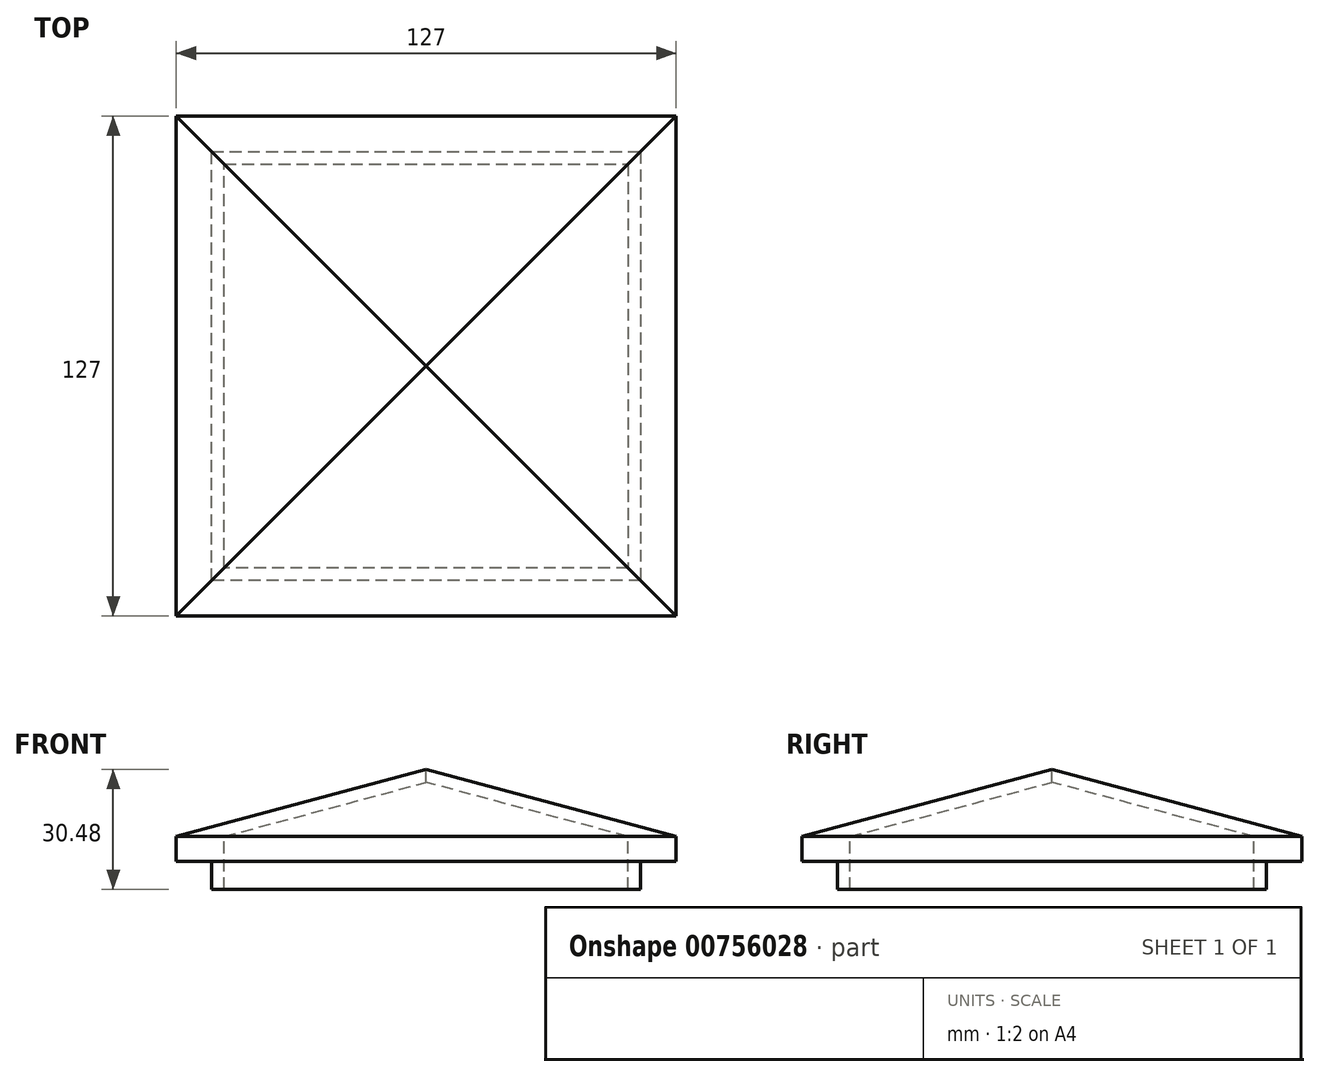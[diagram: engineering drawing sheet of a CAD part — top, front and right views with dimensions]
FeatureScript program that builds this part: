
annotation { "Feature Type Name" : "Feature", "Feature Type Description" : "" }
export const myFeature = defineFeature(function(context is Context, id is Id, definition is map)
    precondition{}
    {
        {
            var Q0;
            Q0=qCreatedBy(makeId("Front.planeOp"),FACE);
            var sketch = newSketch(context, id + "F0", { "sketchPlane" : qUnion([Q0])});
            skLineSegment(sketch, "E0", {"start": v(0, 30.48) * mm, "end": v(63.5, 13.47) * mm});
            skLineSegment(sketch, "E1", {"start": v(63.5, 13.47) * mm, "end": v(63.5, 7.12) * mm});
            skLineSegment(sketch, "E2", {"start": v(63.5, 7.12) * mm, "end": v(54.48, 7.12) * mm});
            skLineSegment(sketch, "E3", {"start": v(54.48, 7.12) * mm, "end": v(54.48, 0) * mm});
            skLineSegment(sketch, "E4", {"start": v(54.48, 0) * mm, "end": v(51.3, 0) * mm});
            skLineSegment(sketch, "E5", {"start": v(51.3, 0) * mm, "end": v(51.3, 13.45) * mm});
            skLineSegment(sketch, "E6", {"start": v(51.3, 13.45) * mm, "end": v(0, 27.2) * mm});
            skLineSegment(sketch, "E7", {"start": v(0, 27.2) * mm, "end": v(0, 30.48) * mm});
            skSolve(sketch);
        }
        {
            var Q0;
            Q0=makeQuery(id+"F0.imprint","IMPRINT",FACE,{"disambiguationData":[TD([[makeQuery(id+"F0.imprint","IMPRINT",EDGE,{"derivedFrom":sQuery(id+"F0.wireOp",EDGE,"E0")}),-1.0]])]});
            extrude(context, id + "F1", {"entities" : qUnion([Q0]), "oppositeDirection" : true, "depth" : 63.5 * mm, "offsetDistance" : 25.4 * mm});
        }
        {
            var Q0;
            Q0=qCreatedBy(makeId("Top.planeOp"),FACE);
            var sketch = newSketch(context, id + "F2", { "sketchPlane" : qUnion([Q0])});
            skLineSegment(sketch, "E8", {"start": v(0, 0) * mm, "end": v(63.5, 63.5) * mm});
            skLineSegment(sketch, "E9", {"start": v(63.5, 63.5) * mm, "end": v(0, 63.5) * mm});
            skLineSegment(sketch, "E10", {"start": v(0, 63.5) * mm, "end": v(0, 0) * mm});
            skSolve(sketch);
        }
        {
            var Q0;
            Q0 = qSketchRegion(id + "F2", true);
            extrude(context, id + "F3", {"entities" : qUnion([Q0]), "operationType" : NewBodyOperationType.REMOVE, "endBound" : BoundingType.THROUGH_ALL, "depth" : 25.4 * mm, "offsetDistance" : 25.4 * mm});
        }
        {
            var Q0;
            Q0=makeQuery(id+"F1.opExtrude","SWEPT_BODY",BODY,{"disambiguationData":[OSD([sQuery(id+"F0.wireOp",EDGE,"E0"),sQuery(id+"F0.wireOp",EDGE,"E1"),sQuery(id+"F0.wireOp",EDGE,"E2"),sQuery(id+"F0.wireOp",EDGE,"E3"),sQuery(id+"F0.wireOp",EDGE,"E4"),sQuery(id+"F0.wireOp",EDGE,"E5"),sQuery(id+"F0.wireOp",EDGE,"E6"),sQuery(id+"F0.wireOp",EDGE,"E7")])]});
            var Q1;
            Q1=qCreatedBy(makeId("Front.planeOp"),FACE);
            mirror(context, id + "F4", {"operationType" : NewBodyOperationType.ADD, "entities" : qUnion([Q0]), "mirrorPlane" : qUnion([Q1])});
        }
        {
            var Q0;
            Q0=makeQuery(id+"F1.opExtrude","SWEPT_BODY",BODY,{"disambiguationData":[OSD([sQuery(id+"F0.wireOp",EDGE,"E0"),sQuery(id+"F0.wireOp",EDGE,"E1"),sQuery(id+"F0.wireOp",EDGE,"E2"),sQuery(id+"F0.wireOp",EDGE,"E3"),sQuery(id+"F0.wireOp",EDGE,"E4"),sQuery(id+"F0.wireOp",EDGE,"E5"),sQuery(id+"F0.wireOp",EDGE,"E6"),sQuery(id+"F0.wireOp",EDGE,"E7")])]});
            var Q1;
            {var subQ0=makeQuery(id+"F3.boolean.opBoolean","MERGE",EDGE,{"derivedFrom":[makeQuery(id+"F1.opExtrude","CAP_EDGE",EDGE,{"disambiguationData":[OSD([sQuery(id+"F0.wireOp",EDGE,"E7")])],"isStart":true}),makeQuery(id+"F3.opExtrude","SWEPT_EDGE",EDGE,{"disambiguationData":[OSD([sQuery(id+"F2.wireOp",EDGE,"E8"),sQuery(id+"F2.wireOp",EDGE,"E10")])]})]});Q1=makeQuery(id+"F4.boolean.opBoolean","MERGE",EDGE,{"derivedFrom":[subQ0,makeQuery(id+"F4.opPattern","COPY",EDGE,{"derivedFrom":subQ0,"instanceName":"1"})]});}
            circularPattern(context, id + "F5", {"entities" : qUnion([Q0]), "axis" : qUnion([Q1]), "angle" : 360 * degree, "instanceCount" : 4, "equalSpace" : true});
        }
    });
